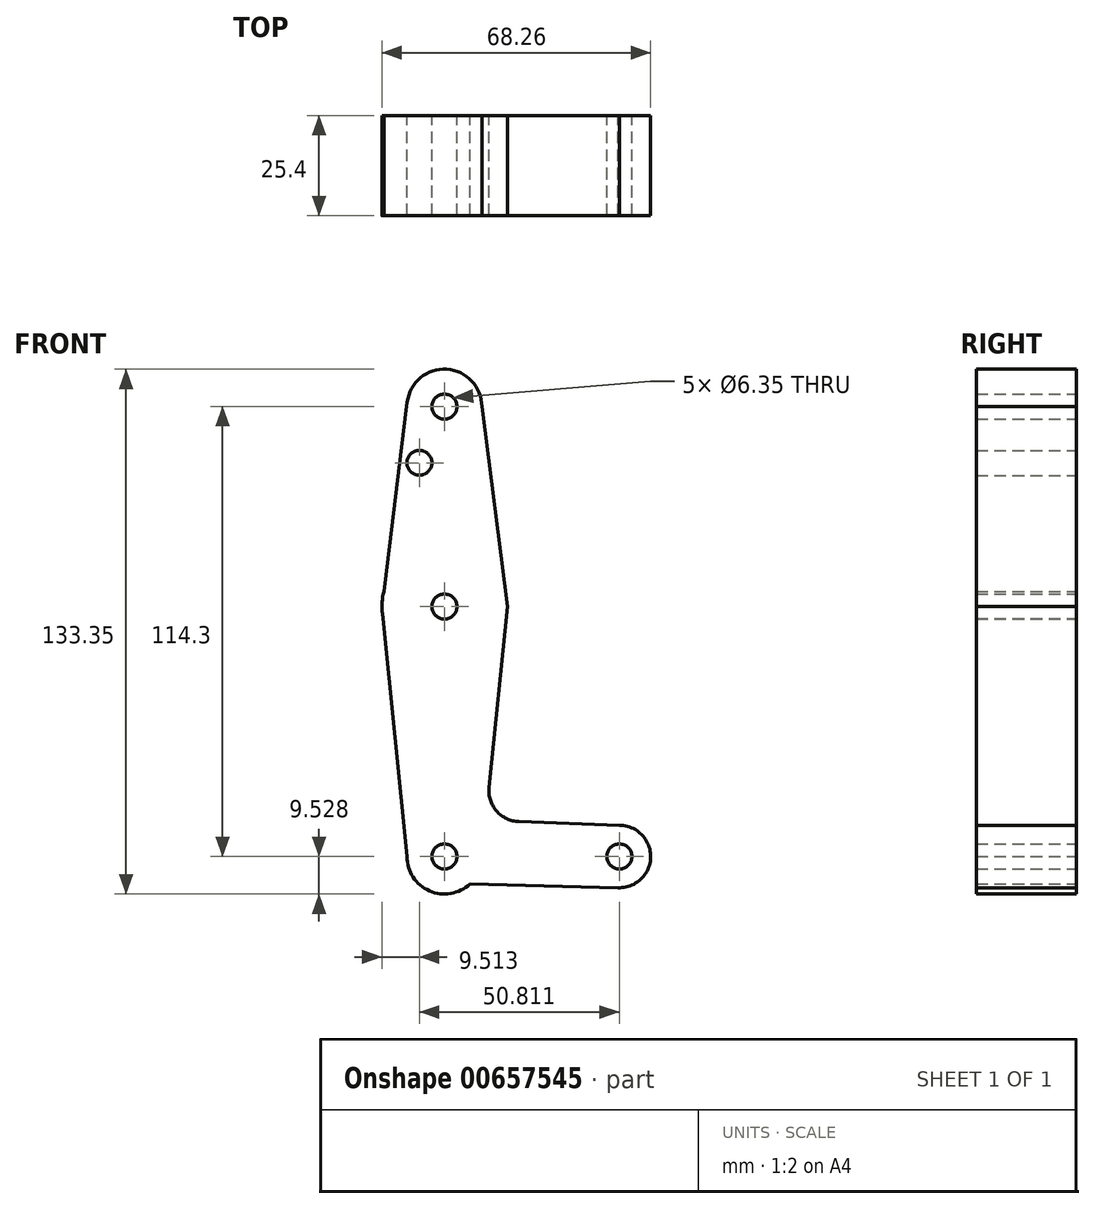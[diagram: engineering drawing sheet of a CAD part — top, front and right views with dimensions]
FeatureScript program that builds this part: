
annotation { "Feature Type Name" : "Feature", "Feature Type Description" : "" }
export const myFeature = defineFeature(function(context is Context, id is Id, definition is map)
    precondition{}
    {
        {
            var Q0;
            Q0=qCreatedBy(makeId("Front.planeOp"),FACE);
            var sketch = newSketch(context, id + "F0", { "sketchPlane" : qUnion([Q0])});
            skLineSegment(sketch, "E0", {"start": v(-322.78, -31.1) * mm, "end": v(-322.78, -145.4) * mm, "construction": true});
            skLineSegment(sketch, "E1", {"start": v(-322.78, -145.4) * mm, "end": v(-278.33, -145.4) * mm, "construction": true});
            skCircle(sketch, "E2", {"center": v(-322.78, -31.1) * mm, "radius": 9.53 * mm});
            skCircle(sketch, "E3", {"center": v(-322.78, -81.9) * mm, "radius": 15.88 * mm});
            skCircle(sketch, "E4", {"center": v(-322.78, -145.4) * mm, "radius": 9.53 * mm});
            skCircle(sketch, "E5", {"center": v(-278.33, -145.4) * mm, "radius": 7.94 * mm});
            skLineSegment(sketch, "E6", {"start": v(-338.17, -78) * mm, "end": v(-338.65, -81.9) * mm});
            skLineSegment(sketch, "E7", {"start": v(-338.65, -81.9) * mm, "end": v(-338.17, -78) * mm});
            skLineSegment(sketch, "E8", {"start": v(-307.03, -79.88) * mm, "end": v(-306.77, -81.9) * mm});
            skLineSegment(sketch, "E9", {"start": v(-338.65, -82.01) * mm, "end": v(-332.3, -145.4) * mm});
            skLineSegment(sketch, "E10", {"start": v(-306.77, -81.9) * mm, "end": v(-311.45, -127.8) * mm});
            skLineSegment(sketch, "E11", {"start": v(-332.23, -29.92) * mm, "end": v(-338.65, -81.9) * mm});
            skLineSegment(sketch, "E12", {"start": v(-303.83, -136.54) * mm, "end": v(-278.33, -137.45) * mm});
            skLineSegment(sketch, "E13", {"start": v(-316.27, -152.35) * mm, "end": v(-278.33, -153.33) * mm});
            skCircle(sketch, "E14", {"center": v(-322.78, -31.1) * mm, "radius": 3.18 * mm});
            skCircle(sketch, "E15", {"center": v(-322.78, -81.9) * mm, "radius": 3.18 * mm});
            skCircle(sketch, "E16", {"center": v(-322.78, -145.4) * mm, "radius": 3.18 * mm});
            skCircle(sketch, "E17", {"center": v(-278.33, -145.4) * mm, "radius": 3.18 * mm});
            skPoint(sketch, "E18.orphan", {"position": v(-313.25, -31.1) * mm});
            skLineSegment(sketch, "E19", {"start": v(-313.25, -31.1) * mm, "end": v(-307.03, -79.88) * mm});
            skCircle(sketch, "E20", {"center": v(-329.14, -45.37) * mm, "radius": 3.18 * mm});
            skPoint(sketch, "E20.second.point", {"position": v(-325.99, -45.77) * mm});
            skPoint(sketch, "E20.third.point", {"position": v(-326, -45.9) * mm});
            skArc(sketch, "E21.filletArc", {"start": v(-311.45, -127.8) * mm, "mid": v(-309.54, -133.82) * mm, "end": v(-303.83, -136.54) * mm});
            skSolve(sketch);
        }
        {
            var Q0;
            Q0 = qSketchRegion(id + "F0", true);
            extrude(context, id + "F1", {"entities" : qUnion([Q0]), "depth" : 25.4 * mm, "offsetDistance" : 25.4 * mm});
        }
    });
